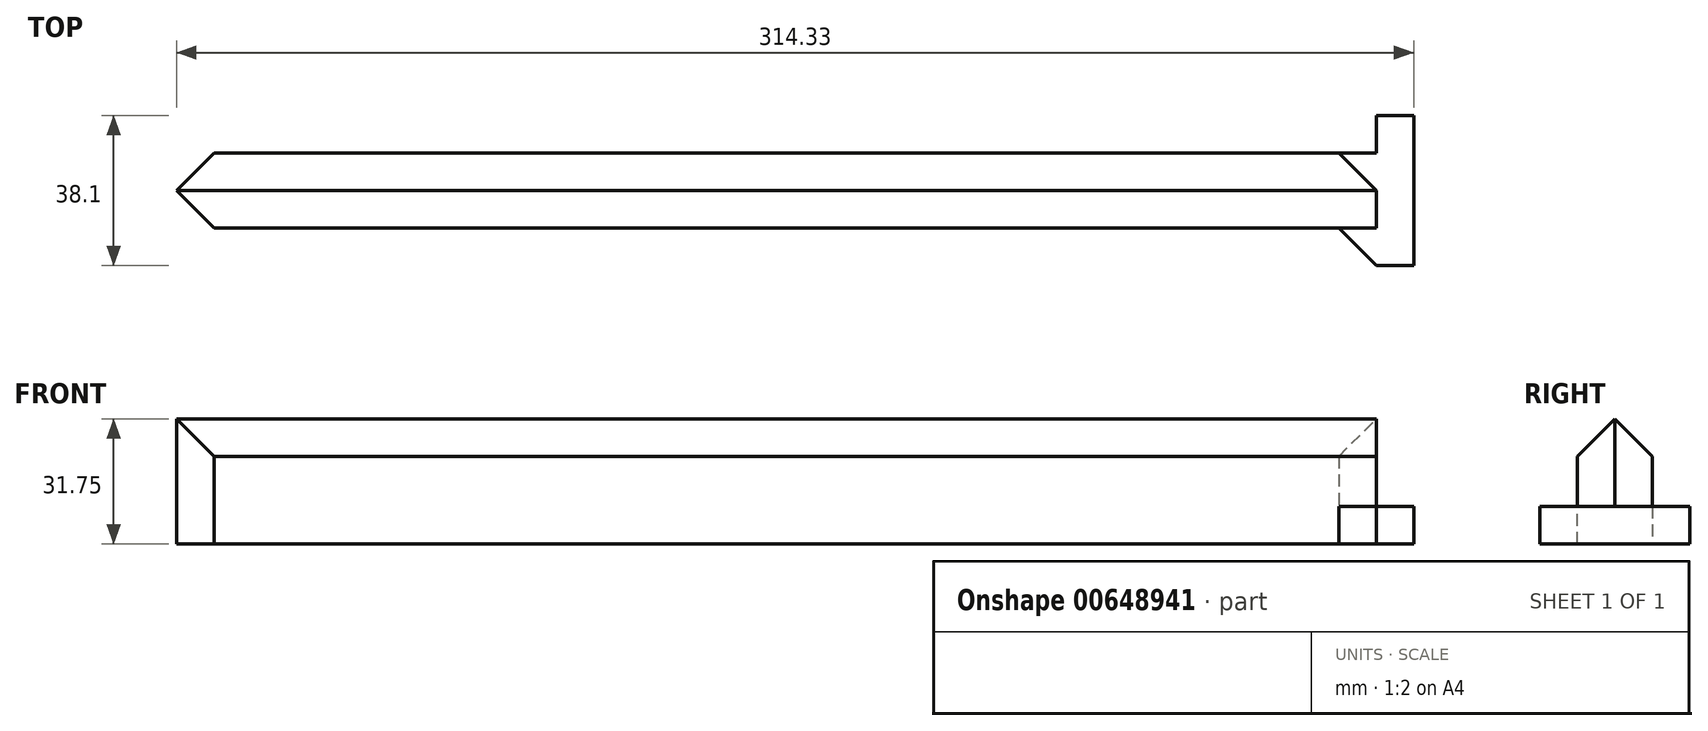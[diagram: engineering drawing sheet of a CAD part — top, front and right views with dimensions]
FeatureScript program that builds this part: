
annotation { "Feature Type Name" : "Feature", "Feature Type Description" : "" }
export const myFeature = defineFeature(function(context is Context, id is Id, definition is map)
    precondition{}
    {
        {
            var Q0;
            Q0=qCreatedBy(makeId("Top.planeOp"),FACE);
            var sketch = newSketch(context, id + "F0", { "sketchPlane" : qUnion([Q0])});
            skLineSegment(sketch, "E0.bottom", {"start": v(-152.4, -9.53) * mm, "end": v(152.4, -9.53) * mm});
            skLineSegment(sketch, "E0.top", {"start": v(-152.4, 9.53) * mm, "end": v(152.4, 9.53) * mm});
            skLineSegment(sketch, "E0.left", {"start": v(-152.4, -9.53) * mm, "end": v(-152.4, 9.53) * mm});
            skLineSegment(sketch, "E0.right", {"start": v(152.4, -9.53) * mm, "end": v(152.4, 9.53) * mm});
            skPoint(sketch, "E0.middle", {"position": v(0, 0) * mm});
            skSolve(sketch);
        }
        {
            var Q0;
            Q0=makeQuery(id+"F0.imprint","IMPRINT",FACE,{"disambiguationData":[TD([[makeQuery(id+"F0.imprint","IMPRINT",EDGE,{"derivedFrom":sQuery(id+"F0.wireOp",EDGE,"E0.bottom")}),1.0]])]});
            extrude(context, id + "F1", {"entities" : qUnion([Q0]), "depth" : 31.75 * mm, "offsetDistance" : 25 * mm});
        }
        {
            var Q0;
            Q0=makeQuery(id+"F1.opExtrude","CAP_EDGE",EDGE,{"disambiguationData":[OSD([sQuery(id+"F0.wireOp",EDGE,"E0.bottom")])],"isStart":false});
            var Q1;
            Q1=makeQuery(id+"F1.opExtrude","CAP_EDGE",EDGE,{"disambiguationData":[OSD([sQuery(id+"F0.wireOp",EDGE,"E0.top")])],"isStart":false});
            chamfer(context, id + "F2", {"entities" : qUnion([Q0, Q1]), "width" : 9.52 * mm, "tangentPropagation" : true});
        }
        {
            var Q0;
            Q0=makeQuery(id+"F1.opExtrude","SWEPT_FACE",FACE,{"disambiguationData":[OSD([sQuery(id+"F0.wireOp",EDGE,"E0.right")])]});
            var sketch = newSketch(context, id + "F3", { "sketchPlane" : qUnion([Q0])});
            skLineSegment(sketch, "E1.bottom", {"start": v(19.05, 0) * mm, "end": v(-19.05, 0) * mm});
            skLineSegment(sketch, "E1.top", {"start": v(19.05, 9.53) * mm, "end": v(-19.05, 9.53) * mm});
            skLineSegment(sketch, "E1.left", {"start": v(19.05, 0) * mm, "end": v(19.05, 9.53) * mm});
            skLineSegment(sketch, "E1.right", {"start": v(-19.05, 0) * mm, "end": v(-19.05, 9.53) * mm});
            skPoint(sketch, "E1.middle", {"position": v(0, 4.76) * mm});
            skSolve(sketch);
        }
        {
            var Q0;
            Q0 = qSketchRegion(id + "F3", true);
            extrude(context, id + "F4", {"entities" : qUnion([Q0]), "operationType" : NewBodyOperationType.ADD, "depth" : 9.52 * mm, "offsetDistance" : 25.4 * mm});
        }
        {
            var Q0;
            {var subQ0=sQuery(id+"F0.wireOp",EDGE,"E0.top");Q0=makeQuery(id+"FstTbWVVVNUrylG_1.1.F4.boolean.opBoolean","SPLIT",EDGE,{"disambiguationData":[topologyDisambiguationEdgeConnected([makeQuery(id+"FstTbWVVVNUrylG_1.1.F4.opExtrude","CAP_FACE",FACE,{"disambiguationData":[OSD([sQuery(id+"F3.wireOp",EDGE,"E1.bottom"),sQuery(id+"F3.wireOp",EDGE,"E1.top"),sQuery(id+"F3.wireOp",EDGE,"E1.left"),sQuery(id+"F3.wireOp",EDGE,"E1.right")])],"isStart":true})])],"derivedFrom":makeQuery(id+"F1.opExtrude","SWEPT_EDGE",EDGE,{"disambiguationData":[OSD([subQ0,sQuery(id+"F0.wireOp",EDGE,"E0.left")])]})});}
            var Q1;
            {var subQ0=sQuery(id+"F0.wireOp",EDGE,"E0.bottom");Q1=makeQuery(id+"FstTbWVVVNUrylG_1.1.F4.boolean.opBoolean","SPLIT",EDGE,{"disambiguationData":[topologyDisambiguationEdgeConnected([makeQuery(id+"FstTbWVVVNUrylG_1.1.F4.opExtrude","CAP_FACE",FACE,{"disambiguationData":[OSD([sQuery(id+"F3.wireOp",EDGE,"E1.bottom"),sQuery(id+"F3.wireOp",EDGE,"E1.top"),sQuery(id+"F3.wireOp",EDGE,"E1.left"),sQuery(id+"F3.wireOp",EDGE,"E1.right")])],"isStart":true})])],"derivedFrom":makeQuery(id+"F1.opExtrude","SWEPT_EDGE",EDGE,{"disambiguationData":[OSD([subQ0,sQuery(id+"F0.wireOp",EDGE,"E0.left")])]})});}
            var Q2;
            {var subQ0=sQuery(id+"F0.wireOp",EDGE,"E0.bottom");Q2=makeQuery(id+"F4.boolean.opBoolean","SPLIT",EDGE,{"disambiguationData":[topologyDisambiguationEdgeConnected([makeQuery(id+"F4.opExtrude","CAP_FACE",FACE,{"disambiguationData":[OSD([sQuery(id+"F3.wireOp",EDGE,"E1.bottom"),sQuery(id+"F3.wireOp",EDGE,"E1.top"),sQuery(id+"F3.wireOp",EDGE,"E1.left"),sQuery(id+"F3.wireOp",EDGE,"E1.right")])],"isStart":true})])],"derivedFrom":makeQuery(id+"F1.opExtrude","SWEPT_EDGE",EDGE,{"disambiguationData":[OSD([subQ0,sQuery(id+"F0.wireOp",EDGE,"E0.right")])]})});}
            var Q3;
            {var subQ0=sQuery(id+"F0.wireOp",EDGE,"E0.top");Q3=makeQuery(id+"F4.boolean.opBoolean","SPLIT",EDGE,{"disambiguationData":[topologyDisambiguationEdgeConnected([makeQuery(id+"F4.opExtrude","CAP_FACE",FACE,{"disambiguationData":[OSD([sQuery(id+"F3.wireOp",EDGE,"E1.bottom"),sQuery(id+"F3.wireOp",EDGE,"E1.top"),sQuery(id+"F3.wireOp",EDGE,"E1.left"),sQuery(id+"F3.wireOp",EDGE,"E1.right")])],"isStart":true})])],"derivedFrom":makeQuery(id+"F1.opExtrude","SWEPT_EDGE",EDGE,{"disambiguationData":[OSD([subQ0,sQuery(id+"F0.wireOp",EDGE,"E0.right")])]})});}
            chamfer(context, id + "F5", {"entities" : qUnion([Q0, Q1, Q2, Q3]), "width" : 9.52 * mm, "tangentPropagation" : true});
        }
    });
